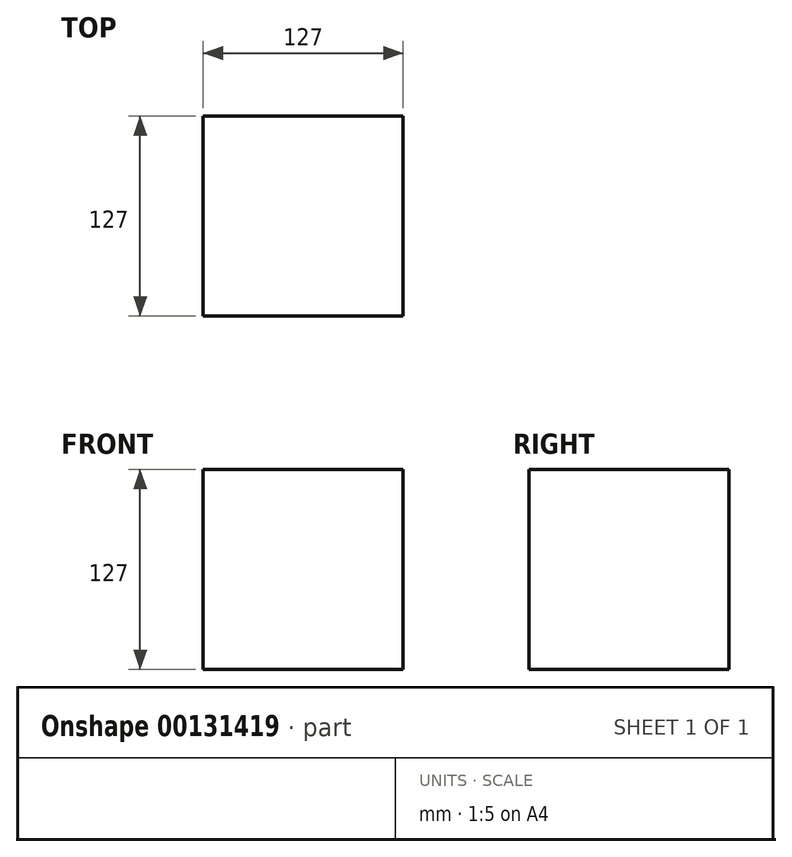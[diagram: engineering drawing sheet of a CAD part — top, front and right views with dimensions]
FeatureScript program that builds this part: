
annotation { "Feature Type Name" : "Feature", "Feature Type Description" : "" }
export const myFeature = defineFeature(function(context is Context, id is Id, definition is map)
    precondition{}
    {
        {
            var Q0;
            Q0=qCreatedBy(makeId("Front.planeOp"),FACE);
            var sketch = newSketch(context, id + "F0", { "sketchPlane" : qUnion([Q0])});
            skLineSegment(sketch, "E0.bottom", {"start": v(-63.5, 63.5) * mm, "end": v(63.5, 63.5) * mm});
            skLineSegment(sketch, "E0.top", {"start": v(-63.5, -63.5) * mm, "end": v(63.5, -63.5) * mm});
            skLineSegment(sketch, "E0.left", {"start": v(-63.5, 63.5) * mm, "end": v(-63.5, -63.5) * mm});
            skLineSegment(sketch, "E0.right", {"start": v(63.5, 63.5) * mm, "end": v(63.5, -63.5) * mm});
            skPoint(sketch, "E0.middle", {"position": v(0, 0) * mm});
            skSolve(sketch);
        }
        {
            var Q0;
            Q0=makeQuery(id+"F0.imprint","IMPRINT",FACE,{"disambiguationData":[TD([[makeQuery(id+"F0.imprint","IMPRINT",EDGE,{"derivedFrom":sQuery(id+"F0.wireOp",EDGE,"E0.bottom")}),-1.0]])]});
            extrude(context, id + "F1", {"entities" : qUnion([Q0]), "endBound" : BoundingType.SYMMETRIC, "depth" : 127 * mm});
        }
    });
